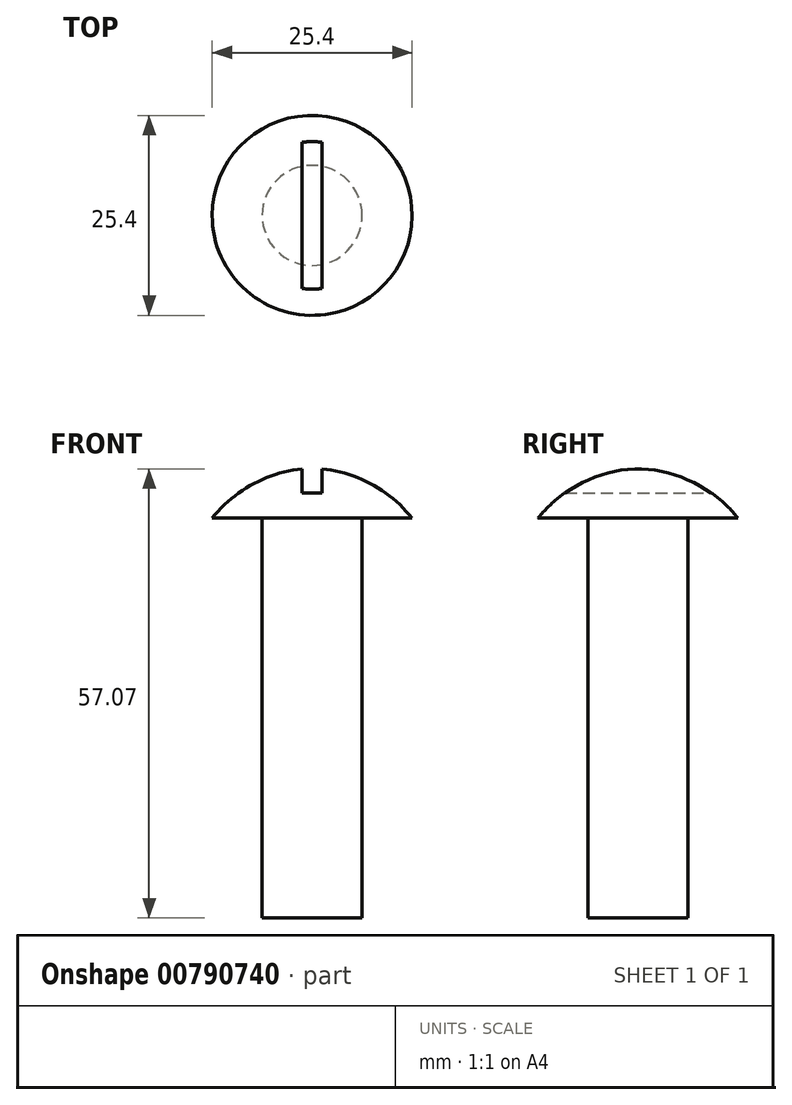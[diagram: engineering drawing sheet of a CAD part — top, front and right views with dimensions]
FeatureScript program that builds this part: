
annotation { "Feature Type Name" : "Feature", "Feature Type Description" : "" }
export const myFeature = defineFeature(function(context is Context, id is Id, definition is map)
    precondition{}
    {
        {
            var Q0;
            Q0=qCreatedBy(makeId("Front.planeOp"),FACE);
            var sketch = newSketch(context, id + "F0", { "sketchPlane" : qUnion([Q0])});
            skLineSegment(sketch, "E0", {"start": v(0, 0) * mm, "end": v(0, 13.49) * mm, "construction": true});
            skLineSegment(sketch, "E1", {"start": v(0, 0) * mm, "end": v(12.7, 0) * mm});
            skLineSegment(sketch, "E2", {"start": v(0, 0) * mm, "end": v(0, 6.35) * mm});
            skArc(sketch, "E3", {"start": v(12.7, 0) * mm, "mid": v(7.05, 4.58) * mm, "end": v(0, 6.35) * mm});
            skLineSegment(sketch, "E4.bottom", {"start": v(1.27, 3.17) * mm, "end": v(-1.27, 3.17) * mm});
            skLineSegment(sketch, "E4.top", {"start": v(1.27, 9.53) * mm, "end": v(-1.27, 9.53) * mm});
            skLineSegment(sketch, "E4.left", {"start": v(1.27, 3.17) * mm, "end": v(1.27, 9.53) * mm});
            skLineSegment(sketch, "E4.right", {"start": v(-1.27, 3.17) * mm, "end": v(-1.27, 9.53) * mm});
            skPoint(sketch, "E4.middle", {"position": v(0, 6.35) * mm});
            skSolve(sketch);
        }
        {
            var Q0;
            Q0=makeQuery(id+"F0.imprint","IMPRINT",FACE,{"disambiguationData":[TD([[makeQuery(id+"F0.imprint","IMPRINT",EDGE,{"derivedFrom":sQuery(id+"F0.wireOp",EDGE,"E1")}),1.0]])]});
            var Q1;
            Q1=sQuery(id+"F0.wireOp",EDGE,"E2");
            revolve(context, id + "F1", {"surfaceOperationType" : NewSurfaceOperationType.NEW, "entities" : qUnion([Q0]), "axis" : qUnion([Q1]), "revolveType" : RevolveType.FULL});
        }
        {
            var Q0;
            {var subQ8=sQuery(id+"F0.wireOp",EDGE,"E4.top");Q0=makeQuery(id+"F0.imprint","IMPRINT",FACE,{"disambiguationData":[TD([[makeQuery(id+"F0.imprint","IMPRINT",EDGE,{"derivedFrom":subQ8}),1.0]])]});}
            var Q1;
            {var subQ0=sQuery(id+"F0.wireOp",EDGE,"E3");var subQ1=sQuery(id+"F0.wireOp",EDGE,"E2");var subQ2=makeQuery(id+"F0.imprint","INTERSECT",VERTEX,{"derivedFrom":[subQ1,subQ0]});Q1=makeQuery(id+"F0.imprint","IMPRINT",FACE,{"disambiguationData":[TD([[makeQuery(id+"F0.imprint","IMPRINT",EDGE,{"disambiguationData":[TD([[subQ2,1.0]])],"derivedFrom":subQ1}),-1.0]])]});}
            extrude(context, id + "F2", {"entities" : qUnion([Q0, Q1]), "operationType" : NewBodyOperationType.REMOVE, "endBound" : BoundingType.SYMMETRIC, "depth" : 25.4 * mm, "offsetDistance" : 25.4 * mm});
        }
        {
            var Q0;
            Q0=makeQuery(id+"F1.opRevolve","SWEPT_FACE",FACE,{"disambiguationData":[OSD([sQuery(id+"F0.wireOp",EDGE,"E1")])]});
            var sketch = newSketch(context, id + "F3", { "sketchPlane" : qUnion([Q0])});
            skCircle(sketch, "E5", {"center": v(0, 0) * mm, "radius": 6.35 * mm});
            skSolve(sketch);
        }
        {
            var Q0;
            Q0=makeQuery(id+"F3.imprint","IMPRINT",FACE,{"disambiguationData":[TD([[makeQuery(id+"F3.imprint","IMPRINT",EDGE,{"derivedFrom":sQuery(id+"F3.wireOp",EDGE,"E5")}),1.0]])]});
            var Q1;
            Q1=sQuery(id+"F3.wireOp",EDGE,"E5");
            extrude(context, id + "F4", {"entities" : qUnion([Q0]), "surfaceEntities" : qUnion([Q1]), "depth" : 50.8 * mm, "offsetDistance" : 25.4 * mm});
        }
    });
